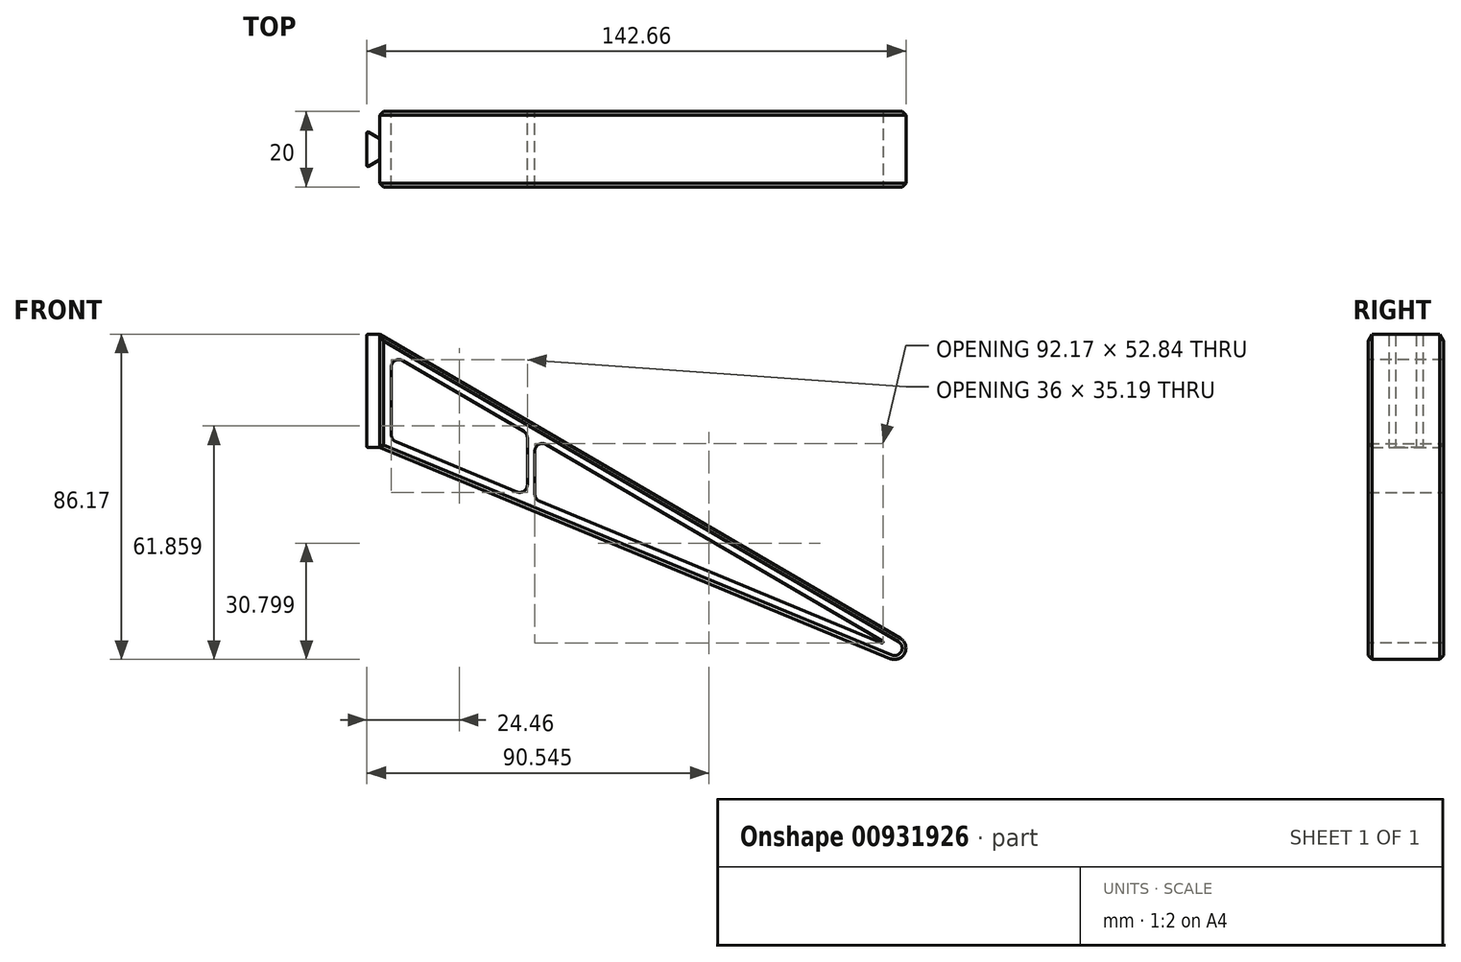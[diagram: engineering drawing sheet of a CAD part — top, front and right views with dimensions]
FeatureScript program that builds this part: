
annotation { "Feature Type Name" : "Feature", "Feature Type Description" : "" }
export const myFeature = defineFeature(function(context is Context, id is Id, definition is map)
    precondition{}
    {
        {
            var Q0;
            Q0=qCreatedBy(makeId("Front.planeOp"),FACE);
            var sketch = newSketch(context, id + "F0", { "sketchPlane" : qUnion([Q0])});
            skLineSegment(sketch, "E0", {"start": v(-46, 0) * mm, "end": v(89.05, -55.94) * mm});
            skLineSegment(sketch, "E1", {"start": v(91.71, -50.58) * mm, "end": v(-46, 30) * mm});
            skLineSegment(sketch, "E2", {"start": v(-46, 30) * mm, "end": v(-46, 0) * mm});
            skPoint(sketch, "E3.visualSharp", {"position": v(129.54, -72.7) * mm});
            skArc(sketch, "E3.filletArc", {"start": v(89.05, -55.94) * mm, "mid": v(92.89, -54.5) * mm, "end": v(91.71, -50.58) * mm});
            skLineSegment(sketch, "E4.0", {"start": v(90.2, -53.17) * mm, "end": v(-43, 24.77) * mm});
            skLineSegment(sketch, "E4.1", {"start": v(90.2, -53.17) * mm, "end": v(90.2, -53.17) * mm});
            skLineSegment(sketch, "E4.2", {"start": v(-43, 2) * mm, "end": v(90.2, -53.17) * mm});
            skLineSegment(sketch, "E4.3", {"start": v(-43, 24.77) * mm, "end": v(-43, 2) * mm});
            skLineSegment(sketch, "E5", {"start": v(-5, -13.74) * mm, "end": v(-5, 2.53) * mm});
            skLineSegment(sketch, "E6", {"start": v(-5, 2.53) * mm, "end": v(-7, 3.7) * mm});
            skLineSegment(sketch, "E7", {"start": v(-7, 3.7) * mm, "end": v(-7, -12.9) * mm});
            skSolve(sketch);
        }
        {
            var Q0;
            Q0=makeQuery(id+"F0.imprint","IMPRINT",FACE,{"disambiguationData":[TD([[makeQuery(id+"F0.imprint","IMPRINT",EDGE,{"derivedFrom":sQuery(id+"F0.wireOp",EDGE,"E0")}),1.0]])]});
            var Q1;
            {var subQ0=sQuery(id+"F0.wireOp",EDGE,"E5");Q1=makeQuery(id+"F0.imprint","IMPRINT",FACE,{"disambiguationData":[TD([[makeQuery(id+"F0.imprint","IMPRINT",EDGE,{"derivedFrom":subQ0}),1.0]])]});}
            extrude(context, id + "F1", {"entities" : qUnion([Q0, Q1]), "depth" : 20 * mm, "offsetDistance" : 25 * mm});
        }
        {
            var Q0;
            Q0=qCreatedBy(makeId("Top.planeOp"),FACE);
            var sketch = newSketch(context, id + "F2", { "sketchPlane" : qUnion([Q0])});
            skLineSegment(sketch, "E8", {"start": v(-46, -7.25) * mm, "end": v(-46, 0) * mm, "construction": true});
            skLineSegment(sketch, "E9", {"start": v(-46, -12.75) * mm, "end": v(-46, -20) * mm, "construction": true});
            skLineSegment(sketch, "E10", {"start": v(-46, -12.75) * mm, "end": v(-46, -7.25) * mm});
            skLineSegment(sketch, "E11", {"start": v(-46, -7.25) * mm, "end": v(-49.46, -5.25) * mm});
            skLineSegment(sketch, "E12", {"start": v(-49.46, -5.25) * mm, "end": v(-49.46, -14.75) * mm});
            skLineSegment(sketch, "E13", {"start": v(-49.46, -14.75) * mm, "end": v(-46, -12.75) * mm});
            skSolve(sketch);
        }
        {
            var Q0;
            Q0=makeQuery(id+"F2.imprint","IMPRINT",FACE,{"disambiguationData":[TD([[makeQuery(id+"F2.imprint","IMPRINT",EDGE,{"derivedFrom":sQuery(id+"F2.wireOp",EDGE,"E10")}),1.0]])]});
            extrude(context, id + "F3", {"entities" : qUnion([Q0]), "operationType" : NewBodyOperationType.ADD, "depth" : 30 * mm, "offsetDistance" : 25 * mm});
        }
        {
            var Q0;
            Q0=makeQuery(id+"F1.opExtrude","SWEPT_EDGE",EDGE,{"disambiguationData":[OSD([sQuery(id+"F0.wireOp",EDGE,"E4.2"),sQuery(id+"F0.wireOp",EDGE,"E7")])]});
            var Q1;
            Q1=makeQuery(id+"F1.opExtrude","SWEPT_EDGE",EDGE,{"disambiguationData":[OSD([sQuery(id+"F0.wireOp",EDGE,"E4.2"),sQuery(id+"F0.wireOp",EDGE,"E4.3")])]});
            var Q2;
            Q2=makeQuery(id+"F1.opExtrude","SWEPT_EDGE",EDGE,{"disambiguationData":[OSD([sQuery(id+"F0.wireOp",EDGE,"E4.0"),sQuery(id+"F0.wireOp",EDGE,"E4.3")])]});
            var Q3;
            Q3=makeQuery(id+"F1.opExtrude","SWEPT_EDGE",EDGE,{"disambiguationData":[OSD([sQuery(id+"F0.wireOp",EDGE,"E4.0"),sQuery(id+"F0.wireOp",EDGE,"E6"),sQuery(id+"F0.wireOp",EDGE,"E7")])]});
            var Q4;
            Q4=makeQuery(id+"F1.opExtrude","SWEPT_EDGE",EDGE,{"disambiguationData":[OSD([sQuery(id+"F0.wireOp",EDGE,"E4.0"),sQuery(id+"F0.wireOp",EDGE,"E5"),sQuery(id+"F0.wireOp",EDGE,"E6")])]});
            var Q5;
            Q5=makeQuery(id+"F1.opExtrude","SWEPT_EDGE",EDGE,{"disambiguationData":[OSD([sQuery(id+"F0.wireOp",EDGE,"E4.2"),sQuery(id+"F0.wireOp",EDGE,"E5")])]});
            fillet(context, id + "F4", {"entities" : qUnion([Q0, Q1, Q2, Q3, Q4, Q5]), "radius" : 2 * mm, "tangentPropagation" : true, "allowEdgeOverflow" : false});
        }
        {
            var Q0;
            Q0=makeQuery(id+"F1.opExtrude","CAP_EDGE",EDGE,{"disambiguationData":[OSD([sQuery(id+"F0.wireOp",EDGE,"E2")])],"isStart":true});
            var Q1;
            Q1=makeQuery(id+"F1.opExtrude","CAP_EDGE",EDGE,{"disambiguationData":[OSD([sQuery(id+"F0.wireOp",EDGE,"E2")])],"isStart":false});
            var Q2;
            Q2=makeQuery(id+"F1.opExtrude","CAP_EDGE",EDGE,{"disambiguationData":[OSD([sQuery(id+"F0.wireOp",EDGE,"E0")])],"isStart":false});
            var Q3;
            Q3=makeQuery(id+"F1.opExtrude","CAP_EDGE",EDGE,{"disambiguationData":[OSD([sQuery(id+"F0.wireOp",EDGE,"E0")])],"isStart":true});
            chamfer(context, id + "F5", {"entities" : qUnion([Q0, Q1, Q2, Q3]), "width" : 1 * mm, "tangentPropagation" : true});
        }
        {
            var Q0;
            Q0=makeQuery(id+"F3.opExtrude","SWEPT_EDGE",EDGE,{"disambiguationData":[OSD([sQuery(id+"F2.wireOp",EDGE,"E12"),sQuery(id+"F2.wireOp",EDGE,"E13")])]});
            var Q1;
            Q1=makeQuery(id+"F3.opExtrude","SWEPT_EDGE",EDGE,{"disambiguationData":[OSD([sQuery(id+"F2.wireOp",EDGE,"E11"),sQuery(id+"F2.wireOp",EDGE,"E12")])]});
            var Q2;
            Q2=makeQuery(id+"F3.opExtrude","SWEPT_FACE",FACE,{"disambiguationData":[OSD([sQuery(id+"F2.wireOp",EDGE,"E12")])]});
            var Q3;
            Q3=makeQuery(id+"F3.opExtrude","CAP_EDGE",EDGE,{"disambiguationData":[OSD([sQuery(id+"F2.wireOp",EDGE,"E12")])],"isStart":true});
            var Q4;
            Q4=makeQuery(id+"F3.opExtrude","CAP_EDGE",EDGE,{"disambiguationData":[OSD([sQuery(id+"F2.wireOp",EDGE,"E13")])],"isStart":false});
            var Q5;
            Q5=makeQuery(id+"F3.opExtrude","CAP_EDGE",EDGE,{"disambiguationData":[OSD([sQuery(id+"F2.wireOp",EDGE,"E11")])],"isStart":false});
            var Q6;
            Q6=makeQuery(id+"F3.opExtrude","CAP_EDGE",EDGE,{"disambiguationData":[OSD([sQuery(id+"F2.wireOp",EDGE,"E11")])],"isStart":true});
            var Q7;
            Q7=makeQuery(id+"F3.opExtrude","CAP_EDGE",EDGE,{"disambiguationData":[OSD([sQuery(id+"F2.wireOp",EDGE,"E13")])],"isStart":true});
            var Q8;
            Q8=makeQuery(id+"F1.opExtrude","SWEPT_EDGE",EDGE,{"disambiguationData":[OSD([sQuery(id+"F0.wireOp",EDGE,"E4.0"),sQuery(id+"F0.wireOp",EDGE,"E4.2")])]});
            fillet(context, id + "F6", {"entities" : qUnion([Q0, Q1, Q2, Q3, Q4, Q5, Q6, Q7, Q8]), "radius" : 0.25 * mm, "tangentPropagation" : true, "allowEdgeOverflow" : false});
        }
    });
